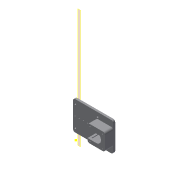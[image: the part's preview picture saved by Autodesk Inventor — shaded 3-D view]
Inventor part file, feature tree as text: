
AUTODESK INVENTOR PART (.ipt)
format: ipt  version: 2019.4 (Build 234330000, 330)  size: 225,792 bytes
history: native  units: mm
features: reference x17, other x10, sketch x6, extrude x3, hole x2, plane x1, fillet x1, pattern_linear x1
ambient origin geometry x8: Origin, YZ Plane, XZ Plane, XY Plane, X Axis, Y Axis, Z Axis, Center Point
bodies: Solid1 (feature_tree)
feature tree (41):
  plane  "Work Plane1"
  extrude  "Extrusion1"  Depth=70.0mm
  extrude  "Extrusion2"  Depth=4.9mm
  sketch  "Sketch3"  dims[d5=4.9mm d6=4.9mm d7=10.0mm]
  extrude  "Extrusion3"  Depth=10.0mm
  fillet  "Fillet1"  Radius=10.0mm
  hole  "Hole1"  [1 undecoded]
  hole  "Hole2"  [1 undecoded]
  pattern_linear  "Rectangular Pattern1"  Spacing1=0.0mm  [1 undecoded]
  sketch  "Sketch1"  dims[d0=50.0mm d2=70.0mm]
  reference  "Reference1"
  reference  "Reference2"
  reference  "Reference3"
  reference  "Reference4"
  reference  "Reference5"
  sketch  "Sketch2"  dims[d3=4.9mm d4=4.9mm]
  reference  "Reference6"
  reference  "Reference7"
  reference  "Reference8"
  reference  "Reference9"
  reference  "Reference10"
  sketch  "Sketch4"  dims[d10=10.0mm d11=11.5mm]
  reference  "Reference11"
  sketch  "Sketch5"  dims[d15=5.0mm d16=0.0mm d17=25.0mm]
  reference  "Reference12"
  reference  "Reference13"
  reference  "Reference14"
  reference  "Reference15"
  reference  "Reference16"
  sketch  "Sketch6"  dims[d18=5.0mm d19=0.0mm d20=0.0mm d21=20.0mm d22=0.0mm d23=5.0mm d24=2.9mm d25=2.9mm d26=2.9mm d27=4.0mm d28=4.0mm d29=4.0mm d30=20.0mm d31=20.0mm d32=2.9mm d33=6.0mm d34=7.0mm d35=3.0mm d36=90.0deg d37=8.0mm d38=0.0mm d39=2.0mm d40=4.0mm d41=20.0mm d42=2.8mm d43=6.0mm d44=8.0mm d45=20.0mm d46=90.0deg d47=8.0mm d48=20.594885mm d49=70.0mm d51=10.0mm]
  reference  "Reference17"
  other  "Assembly_neje_slide_y_wellplateholder_20mmrod.iam"
  other  "Neje_Base_Rod_double_20mm:1"
  other  "Assembly_neje_slide_plate:1"
  other  "Neje_Base_Rod_20mm:1"
  other  "Assembly_neje_slide_y_20mmrod.iam"
  other  "00_NEMA17:1"
  other  "Neje_Rolls_small:1"
  other  "Neje_Rolls_small:4"
  other  "Neje_slide_y_20mmrod_lowerplate:1"
  other  "00_NEMA17:2"
note: 3 required parameter values undecoded (feature->parameter linkage not recoverable at this tier; creation-order binding heuristic only, values carry confidence <= 0.55)
